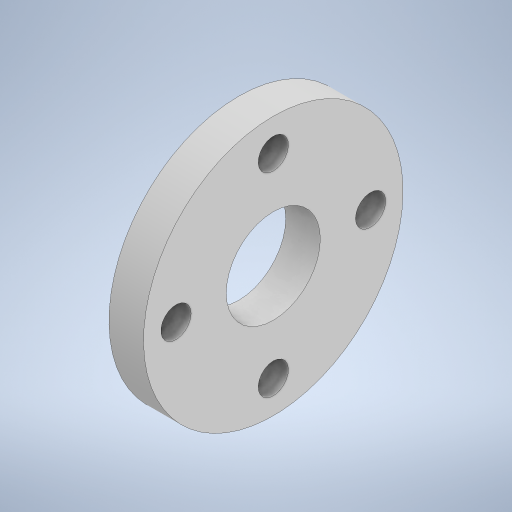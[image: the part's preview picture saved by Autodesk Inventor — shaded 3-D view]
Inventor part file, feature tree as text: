
AUTODESK INVENTOR PART (.ipt)
format: ipt  version: 2023 (Build 270158000, 158)  size: 246,784 bytes
history: native  units: mm
features: sketch x2, revolve x1, extrude x1, pattern_circular x1
ambient origin geometry x8: Origin, YZ Plane, XZ Plane, XY Plane, X Axis, Y Axis, Z Axis, Center Point
bodies: Solido1 (feature_tree)
feature tree (5):
  revolve  "Rivoluzione1"
  extrude  "Estrusione1"  Depth=16.0mm
  pattern_circular  "Serie circolare1"  [2 undecoded]
  sketch  "Schizzo1"
  sketch  "Schizzo2"
note: 2 required parameter values undecoded (feature->parameter linkage not recoverable at this tier; creation-order binding heuristic only, values carry confidence <= 0.55)
